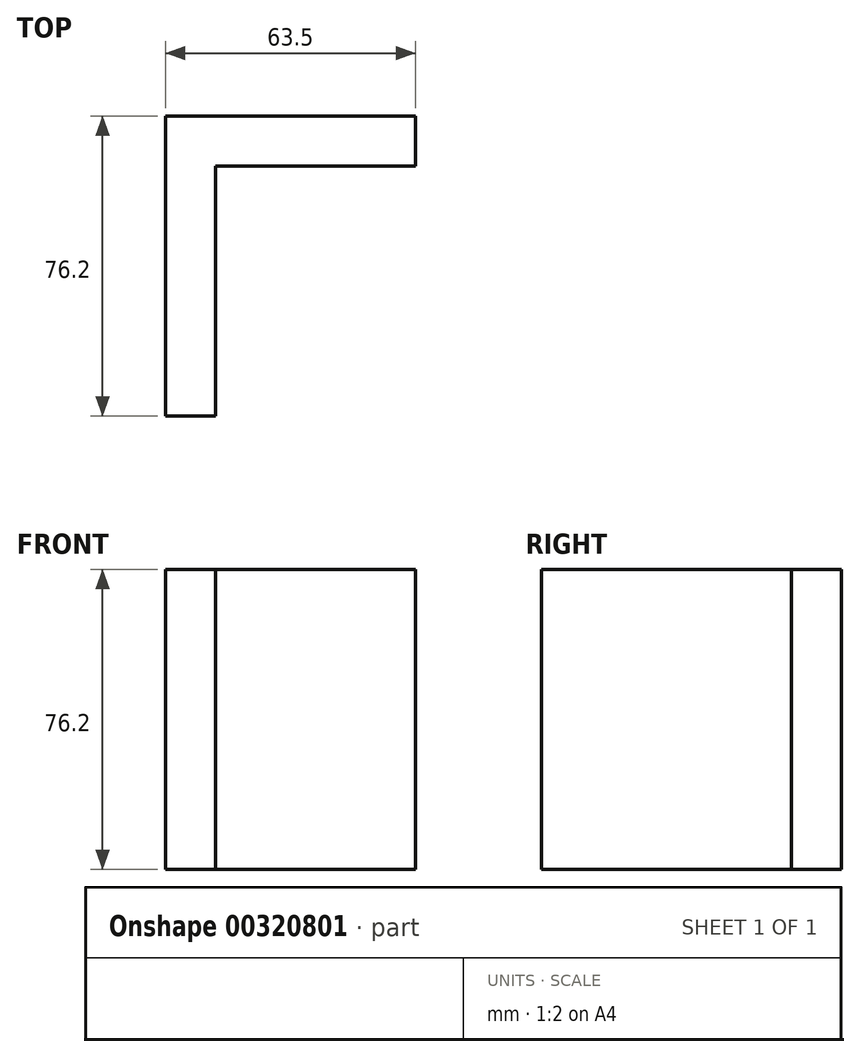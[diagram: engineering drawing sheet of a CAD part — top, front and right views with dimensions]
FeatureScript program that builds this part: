
annotation { "Feature Type Name" : "Feature", "Feature Type Description" : "" }
export const myFeature = defineFeature(function(context is Context, id is Id, definition is map)
    precondition{}
    {
        {
            var Q0;
            Q0=qCreatedBy(makeId("Front.planeOp"),FACE);
            var sketch = newSketch(context, id + "F0", { "sketchPlane" : qUnion([Q0])});
            skLineSegment(sketch, "E0", {"start": v(-45.99, 35.96) * mm, "end": v(-45.99, -40.24) * mm});
            skLineSegment(sketch, "E1", {"start": v(-45.99, -40.24) * mm, "end": v(17.51, -40.24) * mm});
            skLineSegment(sketch, "E2", {"start": v(17.51, -40.24) * mm, "end": v(17.51, 35.96) * mm});
            skLineSegment(sketch, "E3", {"start": v(17.51, 35.96) * mm, "end": v(-45.99, 35.96) * mm});
            skSolve(sketch);
        }
        {
            var Q0;
            Q0=makeQuery(id+"F0.imprint","IMPRINT",FACE,{"disambiguationData":[TD([[makeQuery(id+"F0.imprint","IMPRINT",EDGE,{"derivedFrom":sQuery(id+"F0.wireOp",EDGE,"E0")}),1.0]])]});
            extrude(context, id + "F1", {"entities" : qUnion([Q0]), "depth" : 12.7 * mm});
        }
        {
            var Q0;
            Q0=makeQuery(id+"F1.opExtrude","CAP_FACE",FACE,{"disambiguationData":[OSD([sQuery(id+"F0.wireOp",EDGE,"E0"),sQuery(id+"F0.wireOp",EDGE,"E1"),sQuery(id+"F0.wireOp",EDGE,"E2"),sQuery(id+"F0.wireOp",EDGE,"E3")])],"isStart":false});
            var sketch = newSketch(context, id + "F2", { "sketchPlane" : qUnion([Q0])});
            skLineSegment(sketch, "E4", {"start": v(-45.99, 35.96) * mm, "end": v(-33.29, 35.96) * mm});
            skLineSegment(sketch, "E5", {"start": v(-33.29, 35.96) * mm, "end": v(-33.29, -40.24) * mm});
            skLineSegment(sketch, "E6", {"start": v(-33.29, -40.24) * mm, "end": v(-45.99, -40.24) * mm});
            skLineSegment(sketch, "E7", {"start": v(-45.99, -40.24) * mm, "end": v(-45.99, 35.96) * mm});
            skSolve(sketch);
        }
        {
            var Q0;
            Q0=makeQuery(id+"F2.imprint","IMPRINT",FACE,{"disambiguationData":[TD([[makeQuery(id+"F2.imprint","IMPRINT",EDGE,{"derivedFrom":sQuery(id+"F2.wireOp",EDGE,"E4")}),1.0]])]});
            extrude(context, id + "F3", {"entities" : qUnion([Q0]), "operationType" : NewBodyOperationType.ADD, "depth" : 63.5 * mm});
        }
    });
